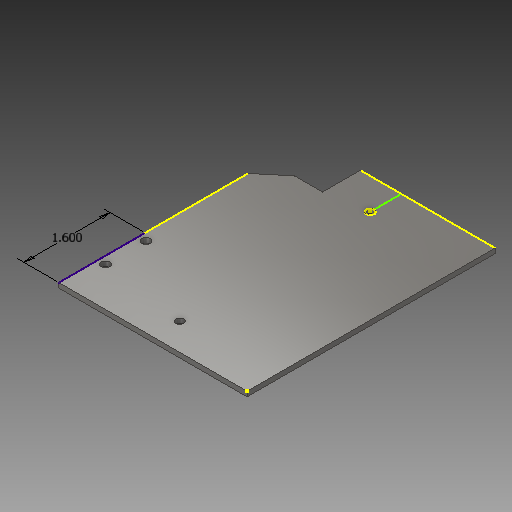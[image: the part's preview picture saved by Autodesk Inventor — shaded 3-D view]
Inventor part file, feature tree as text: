
AUTODESK INVENTOR PART (.ipt)
format: ipt  version: 2017 (Build 210142000, 142)  size: 119,808 bytes
history: native  units: in
note: dims shown in document units (in); Inventor stores cm internally (conversion verified against a paired STEP export)
features: sketch x4, other x4, extrude x2, reference x2
ambient origin geometry x8: Origin, YZ Plane, XZ Plane, XY Plane, X Axis, Y Axis, Z Axis, Center Point
bodies: Solid1 (feature_tree)
feature tree (12):
  extrude  "Extrusion1"  Depth=2.5in
  sketch  "Sketch2"  dims[d2=0.7in d3=0.52in]
  extrude  "Extrusion2"  Depth=0.7in
  sketch  "Sketch4"  dims[d6=3.5in d11=0.09in d12=0.0in d13=1.6in d14=0.75in d15=0.0in]
  sketch  "Sketch1"  dims[d0=4.6in d1=2.5in]
  sketch  "Sketch3"  dims[d4=3.5in]
  reference  "Reference1"
  reference  "Reference2"
  other  "<userpath>\Documents\GitHub\RobotuxCAD\Team Robotux 15-16 Robot Cad Assets\Flywheels.iam"
  other  "Flywheels.iam"
  other  "Flywheel w motor:1"
  other  "am-2875+Banebots+P60+4-1:1"
